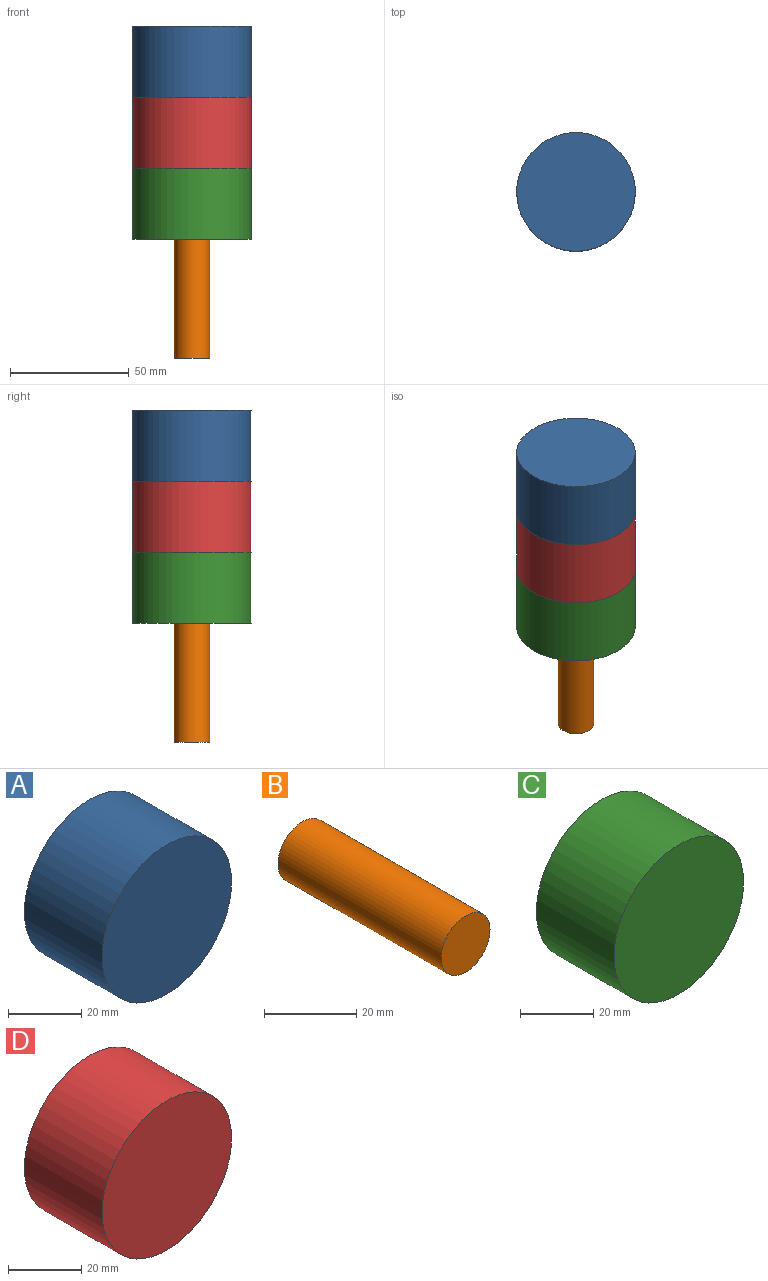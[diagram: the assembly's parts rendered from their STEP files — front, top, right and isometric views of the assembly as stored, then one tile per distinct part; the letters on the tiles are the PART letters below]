
ASSEMBLY  parts=4 mates=3
PART A: 3 faces, bbox 50x30x50 mm
  f0: cylinder r=25mm len=50mm, axis (0,1,0), area 4712.4mm2, adj f1,f2
  f1: plane 50x50mm, normal (0,-1,0), area 1963.5mm2, adj f0
  f2: plane 50x50mm, normal (0,1,0), area 1963.5mm2, adj f0
PART B: 3 faces, bbox 15x50x15 mm
  f0: cylinder r=7.5mm len=50mm, axis (0,1,0), area 2356.2mm2, adj f1,f2
  f1: plane 15x15mm, normal (0,-1,0), area 176.7mm2, adj f0
  f2: plane 15x15mm, normal (0,1,0), area 176.7mm2, adj f0
PART C: 3 faces, bbox 50x30x50 mm
  f0: cylinder r=25mm len=50mm, axis (0,1,0), area 4712.4mm2, adj f1,f2
  f1: plane 50x50mm, normal (0,-1,0), area 1963.5mm2, adj f0
  f2: plane 50x50mm, normal (0,1,0), area 1963.5mm2, adj f0
PART D: 3 faces, bbox 50x30x50 mm
  f0: cylinder r=25mm len=50mm, axis (0,1,0), area 4712.4mm2, adj f1,f2
  f1: plane 50x50mm, normal (0,-1,0), area 1963.5mm2, adj f0
  f2: plane 50x50mm, normal (0,1,0), area 1963.5mm2, adj f0
PLACE A rot(axis=(1,0,0),90deg) t=(-103.81,-84.82,161.07)mm
PLACE B rot(axis=(1,0,0),90deg) t=(-9.75,-3.24,71.07)mm
PLACE C rot(axis=(1,0,0),90deg) t=(-66.98,-36.19,101.07)mm
PLACE D rot(axis=(1,0,0),90deg) t=(-122.83,-14.21,131.07)mm
MATE fastened A.f0 <-> D.f0  axis (0,0,-1) through (-77.77,-55.32,131.07)mm
MATE fastened C.f0 <-> B.f0  axis (0,0,-1) through (-77.77,-55.32,71.07)mm
MATE fastened D.f0 <-> C.f0  axis (0,0,-1) through (-77.77,-55.32,101.07)mm
